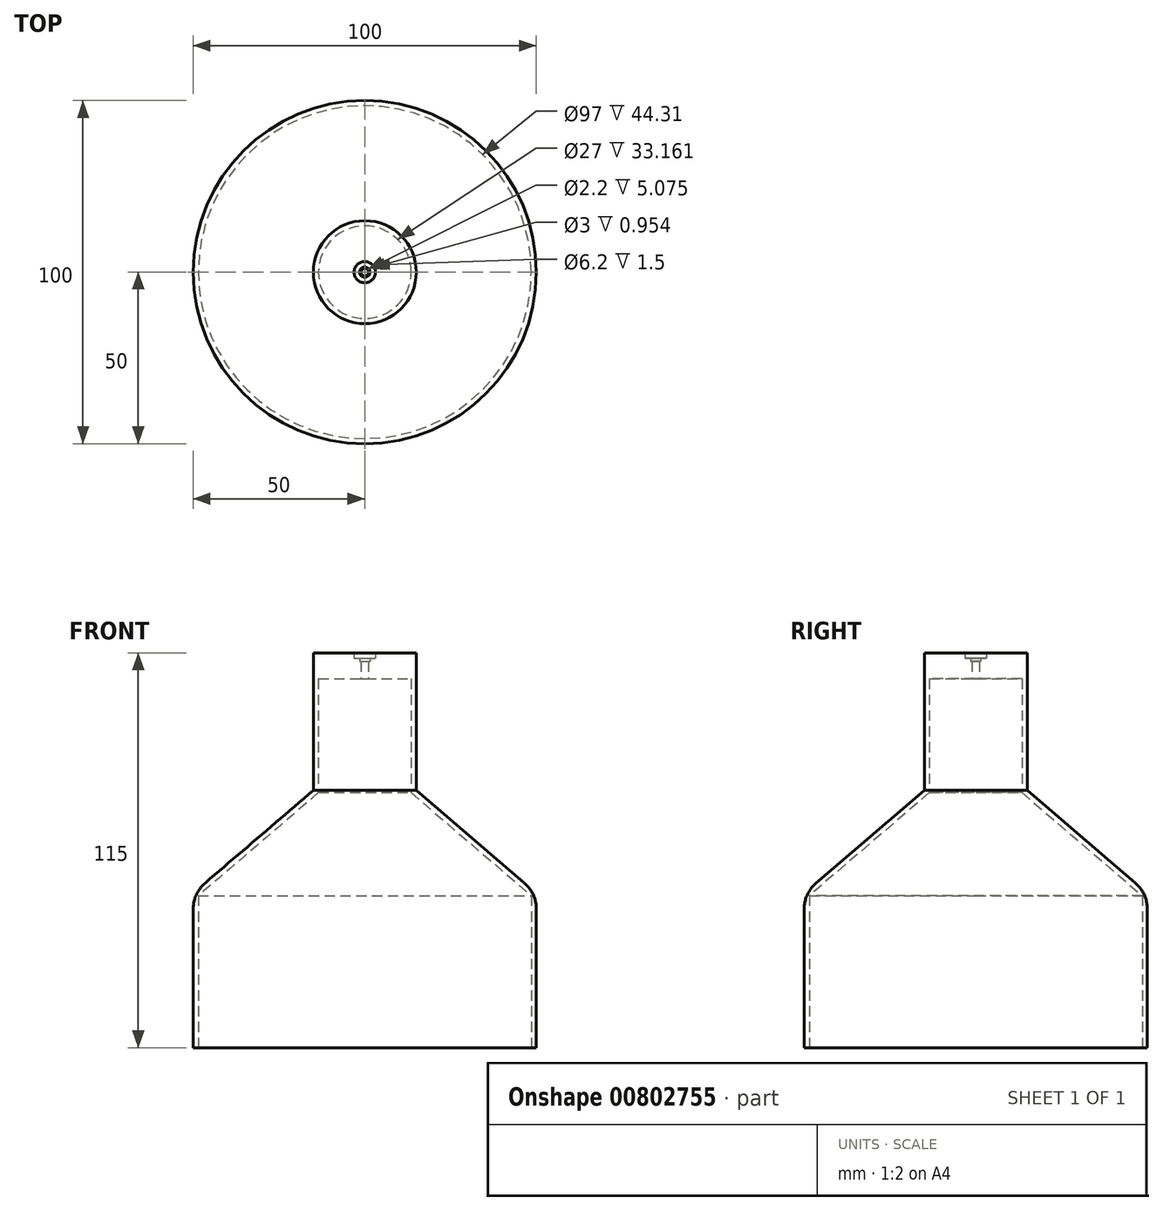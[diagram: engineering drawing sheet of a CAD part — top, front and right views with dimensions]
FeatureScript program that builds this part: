
annotation { "Feature Type Name" : "Feature", "Feature Type Description" : "" }
export const myFeature = defineFeature(function(context is Context, id is Id, definition is map)
    precondition{}
    {
        {
            var Q0;
            Q0=qCreatedBy(makeId("Right.planeOp"),FACE);
            var sketch = newSketch(context, id + "F0", { "sketchPlane" : qUnion([Q0])});
            skLineSegment(sketch, "E0", {"start": v(-48.5, 15) * mm, "end": v(-50, 15) * mm});
            skLineSegment(sketch, "E1", {"start": v(-50, 15) * mm, "end": v(-50, 60) * mm});
            skLineSegment(sketch, "E2", {"start": v(-50, 60) * mm, "end": v(-15, 90) * mm});
            skLineSegment(sketch, "E3", {"start": v(-15, 90) * mm, "end": v(-15, 130) * mm});
            skLineSegment(sketch, "E4", {"start": v(-15, 130) * mm, "end": v(-3.1, 130) * mm});
            skLineSegment(sketch, "E5", {"start": v(-3.1, 130) * mm, "end": v(-3.1, 128.5) * mm});
            skLineSegment(sketch, "E6", {"start": v(-3.1, 128.5) * mm, "end": v(-1.5, 128.5) * mm});
            skLineSegment(sketch, "E7", {"start": v(-1.5, 128.5) * mm, "end": v(-1.5, 127.55) * mm});
            skLineSegment(sketch, "E8", {"start": v(-1.5, 127.55) * mm, "end": v(-1.1, 127.55) * mm});
            skLineSegment(sketch, "E9", {"start": v(-1.1, 127.55) * mm, "end": v(-1.1, 122.47) * mm});
            skLineSegment(sketch, "E10", {"start": v(-1.1, 122.47) * mm, "end": v(-13.5, 122.47) * mm});
            skLineSegment(sketch, "E11.0", {"start": v(-13.5, 89.31) * mm, "end": v(-13.5, 122.47) * mm});
            skLineSegment(sketch, "E11.1", {"start": v(-48.5, 59.31) * mm, "end": v(-13.5, 89.31) * mm});
            skLineSegment(sketch, "E11.2", {"start": v(-48.5, 15) * mm, "end": v(-48.5, 59.31) * mm});
            skLineSegment(sketch, "E12", {"start": v(0, 0) * mm, "end": v(0, 17.95) * mm});
            skSolve(sketch);
        }
        {
            var Q0;
            Q0 = qSketchRegion(id + "F0", true);
            var Q1;
            Q1=sQuery(id+"F0.wireOp",EDGE,"E12");
            revolve(context, id + "F1", {"surfaceOperationType" : NewSurfaceOperationType.NEW, "entities" : qUnion([Q0]), "axis" : qUnion([Q1]), "revolveType" : RevolveType.FULL});
        }
        {
            var Q0;
            Q0=makeQuery(id+"F1.opRevolve","SWEPT_EDGE",EDGE,{"disambiguationData":[OSD([sQuery(id+"F0.wireOp",EDGE,"E1"),sQuery(id+"F0.wireOp",EDGE,"E2")])]});
            fillet(context, id + "F2", {"entities" : qUnion([Q0]), "radius" : 10 * mm, "tangentPropagation" : true, "allowEdgeOverflow" : false});
        }
    });
